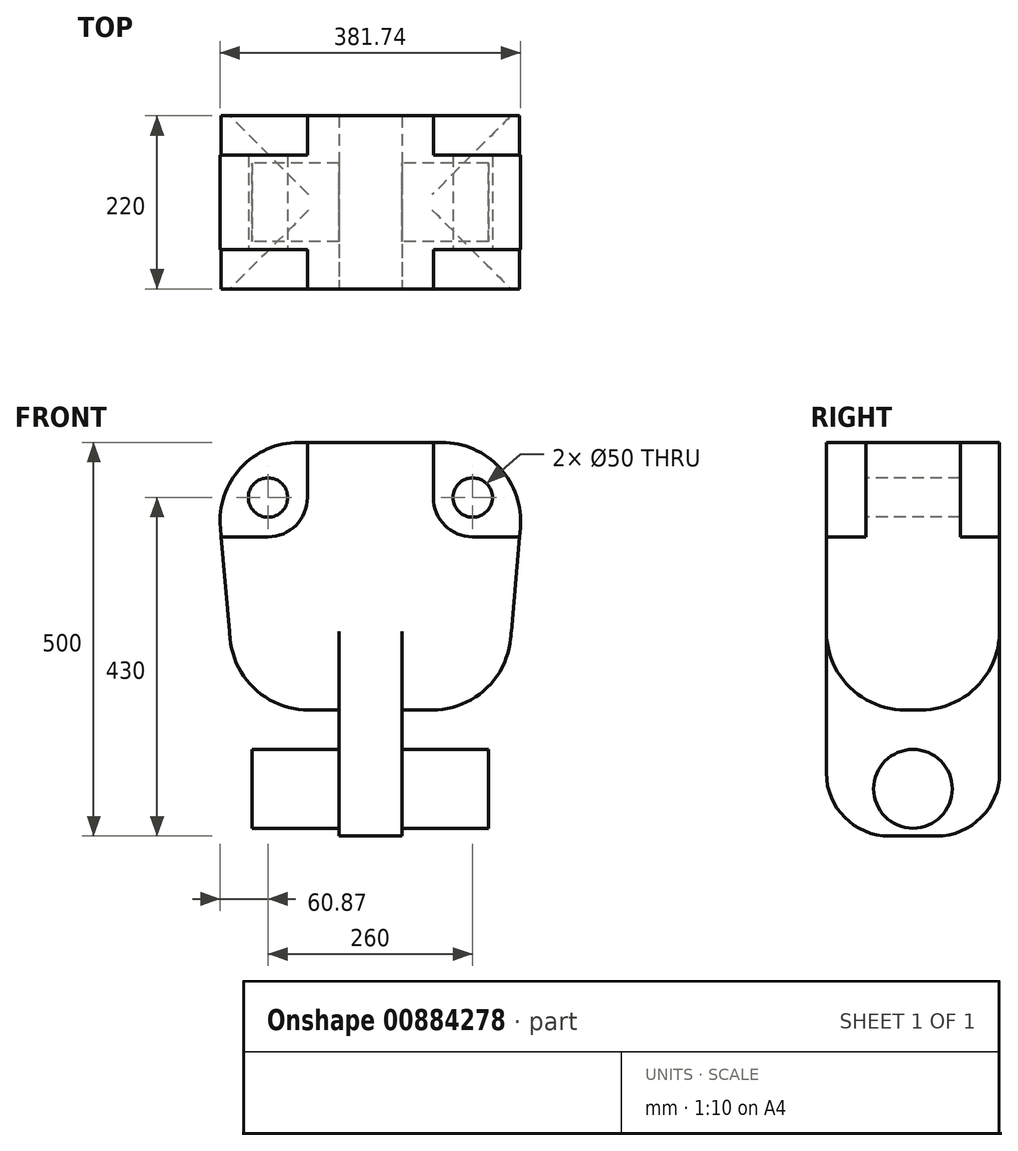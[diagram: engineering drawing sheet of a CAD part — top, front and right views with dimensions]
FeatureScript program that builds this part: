
annotation { "Feature Type Name" : "Feature", "Feature Type Description" : "" }
export const myFeature = defineFeature(function(context is Context, id is Id, definition is map)
    precondition{}
    {
        {
            var Q0;
            Q0=qCreatedBy(makeId("Front.planeOp"),FACE);
            var sketch = newSketch(context, id + "F0", { "sketchPlane" : qUnion([Q0])});
            skLineSegment(sketch, "E0", {"start": v(0, 0) * mm, "end": v(0, 384.02) * mm, "construction": true});
            skLineSegment(sketch, "E1", {"start": v(0, -60) * mm, "end": v(-40, -60) * mm});
            skLineSegment(sketch, "E2", {"start": v(-40, -60) * mm, "end": v(-40, 100) * mm});
            skLineSegment(sketch, "E3", {"start": v(-40, 100) * mm, "end": v(-170.25, 100) * mm});
            skLineSegment(sketch, "E4", {"start": v(-170.25, 100) * mm, "end": v(-200, 440) * mm});
            skLineSegment(sketch, "E5", {"start": v(-200, 440) * mm, "end": v(0, 440) * mm});
            skLineSegment(sketch, "E6.MirrorCS", {"start": v(0, -60) * mm, "end": v(40, -60) * mm});
            skLineSegment(sketch, "E7.MirrorCS", {"start": v(200, 440) * mm, "end": v(0, 440) * mm});
            skLineSegment(sketch, "E8.MirrorCS", {"start": v(40, -60) * mm, "end": v(40, 100) * mm});
            skLineSegment(sketch, "E9.MirrorCS", {"start": v(40, 100) * mm, "end": v(170.25, 100) * mm});
            skLineSegment(sketch, "E10.MirrorCS", {"start": v(170.25, 100) * mm, "end": v(200, 440) * mm});
            skSolve(sketch);
        }
        {
            var Q0;
            Q0 = qSketchRegion(id + "F0", true);
            extrude(context, id + "F1", {"entities" : qUnion([Q0]), "endBound" : BoundingType.SYMMETRIC, "depth" : 220 * mm, "offsetDistance" : 25 * mm});
        }
        {
            var Q0;
            Q0=qCreatedBy(makeId("Front.planeOp"),FACE);
            var sketch = newSketch(context, id + "F2", { "sketchPlane" : qUnion([Q0])});
            skLineSegment(sketch, "E11", {"start": v(4.76, 0) * mm, "end": v(327.19, 0) * mm, "construction": true});
            skLineSegment(sketch, "E12", {"start": v(-150, 50) * mm, "end": v(150, 50) * mm});
            skLineSegment(sketch, "E13", {"start": v(0, 0) * mm, "end": v(0, 285.33) * mm, "construction": true});
            skLineSegment(sketch, "E14", {"start": v(-150, 0) * mm, "end": v(150, 0) * mm});
            skLineSegment(sketch, "E15", {"start": v(-150, 0) * mm, "end": v(-150, 50) * mm});
            skLineSegment(sketch, "E16", {"start": v(150, 0) * mm, "end": v(150, 50) * mm});
            skSolve(sketch);
        }
        {
            var Q0;
            Q0 = qSketchRegion(id + "F2", true);
            var Q1;
            Q1=sQuery(id+"F2.wireOp",EDGE,"E11");
            revolve(context, id + "F3", {"operationType" : NewBodyOperationType.ADD, "surfaceOperationType" : NewSurfaceOperationType.NEW, "entities" : qUnion([Q0]), "axis" : qUnion([Q1]), "revolveType" : RevolveType.FULL});
        }
        {
            var Q0;
            Q0=makeQuery(id+"F1.opExtrude","SWEPT_FACE",FACE,{"disambiguationData":[OSD([sQuery(id+"F0.wireOp",EDGE,"E5"),sQuery(id+"F0.wireOp",EDGE,"E7.MirrorCS")])]});
            var sketch = newSketch(context, id + "F4", { "sketchPlane" : qUnion([Q0])});
            skLineSegment(sketch, "E17.bottom", {"start": v(-200, 110) * mm, "end": v(-80, 110) * mm});
            skLineSegment(sketch, "E17.top", {"start": v(-200, 60) * mm, "end": v(-80, 60) * mm});
            skLineSegment(sketch, "E17.left", {"start": v(-200, 110) * mm, "end": v(-200, 60) * mm});
            skLineSegment(sketch, "E17.right", {"start": v(-80, 110) * mm, "end": v(-80, 60) * mm});
            skLineSegment(sketch, "E18.bottom", {"start": v(-200, -110) * mm, "end": v(-80, -110) * mm});
            skLineSegment(sketch, "E18.top", {"start": v(-200, -60) * mm, "end": v(-80, -60) * mm});
            skLineSegment(sketch, "E18.left", {"start": v(-200, -110) * mm, "end": v(-200, -60) * mm});
            skLineSegment(sketch, "E18.right", {"start": v(-80, -110) * mm, "end": v(-80, -60) * mm});
            skLineSegment(sketch, "E19.bottom", {"start": v(200, -110) * mm, "end": v(80, -110) * mm});
            skLineSegment(sketch, "E19.top", {"start": v(200, -60) * mm, "end": v(80, -60) * mm});
            skLineSegment(sketch, "E19.left", {"start": v(200, -110) * mm, "end": v(200, -60) * mm});
            skLineSegment(sketch, "E19.right", {"start": v(80, -110) * mm, "end": v(80, -60) * mm});
            skLineSegment(sketch, "E20.bottom", {"start": v(200, 110) * mm, "end": v(80, 110) * mm});
            skLineSegment(sketch, "E20.top", {"start": v(200, 60) * mm, "end": v(80, 60) * mm});
            skLineSegment(sketch, "E20.left", {"start": v(200, 110) * mm, "end": v(200, 60) * mm});
            skLineSegment(sketch, "E20.right", {"start": v(80, 110) * mm, "end": v(80, 60) * mm});
            skLineSegment(sketch, "E21", {"start": v(0, 0) * mm, "end": v(276.04, 0) * mm, "construction": true});
            skLineSegment(sketch, "E22", {"start": v(0, 0) * mm, "end": v(0, 138.88) * mm, "construction": true});
            skSolve(sketch);
        }
        {
            var Q0;
            Q0=makeQuery(id+"F4.imprint","IMPRINT",FACE,{"disambiguationData":[TD([[makeQuery(id+"F4.imprint","IMPRINT",EDGE,{"derivedFrom":sQuery(id+"F4.wireOp",EDGE,"E19.bottom")}),-1.0]])]});
            var Q1;
            Q1=makeQuery(id+"F4.imprint","IMPRINT",FACE,{"disambiguationData":[TD([[makeQuery(id+"F4.imprint","IMPRINT",EDGE,{"derivedFrom":sQuery(id+"F4.wireOp",EDGE,"E20.bottom")}),1.0]])]});
            var Q2;
            Q2=makeQuery(id+"F4.imprint","IMPRINT",FACE,{"disambiguationData":[TD([[makeQuery(id+"F4.imprint","IMPRINT",EDGE,{"derivedFrom":sQuery(id+"F4.wireOp",EDGE,"E17.bottom")}),1.0]])]});
            var Q3;
            Q3=makeQuery(id+"F4.imprint","IMPRINT",FACE,{"disambiguationData":[TD([[makeQuery(id+"F4.imprint","IMPRINT",EDGE,{"derivedFrom":sQuery(id+"F4.wireOp",EDGE,"E18.bottom")}),-1.0]])]});
            extrude(context, id + "F5", {"entities" : qUnion([Q0, Q1, Q2, Q3]), "operationType" : NewBodyOperationType.REMOVE, "oppositeDirection" : true, "depth" : 120 * mm, "offsetDistance" : 25 * mm});
        }
        {
            var Q0;
            Q0=makeQuery(id+"F5.boolean.opBoolean","COPY",EDGE,{"derivedFrom":makeQuery(id+"F5.opExtrude","CAP_EDGE",EDGE,{"disambiguationData":[OSD([sQuery(id+"F4.wireOp",EDGE,"E19.right")])],"isStart":false})});
            var Q1;
            Q1=makeQuery(id+"F5.boolean.opBoolean","COPY",EDGE,{"derivedFrom":makeQuery(id+"F5.opExtrude","CAP_EDGE",EDGE,{"disambiguationData":[OSD([sQuery(id+"F4.wireOp",EDGE,"E18.right")])],"isStart":false})});
            var Q2;
            Q2=makeQuery(id+"F5.boolean.opBoolean","COPY",EDGE,{"derivedFrom":makeQuery(id+"F5.opExtrude","CAP_EDGE",EDGE,{"disambiguationData":[OSD([sQuery(id+"F4.wireOp",EDGE,"E17.right")])],"isStart":false})});
            var Q3;
            Q3=makeQuery(id+"F5.boolean.opBoolean","COPY",EDGE,{"derivedFrom":makeQuery(id+"F5.opExtrude","CAP_EDGE",EDGE,{"disambiguationData":[OSD([sQuery(id+"F4.wireOp",EDGE,"E20.right")])],"isStart":false})});
            fillet(context, id + "F6", {"entities" : qUnion([Q0, Q1, Q2, Q3]), "radius" : 50 * mm, "tangentPropagation" : true, "allowEdgeOverflow" : false});
        }
        {
            var Q0;
            Q0=makeQuery(id+"F1.opExtrude","SWEPT_EDGE",EDGE,{"disambiguationData":[OSD([sQuery(id+"F0.wireOp",EDGE,"E7.MirrorCS"),sQuery(id+"F0.wireOp",EDGE,"E10.MirrorCS")])]});
            var Q1;
            Q1=makeQuery(id+"F1.opExtrude","SWEPT_EDGE",EDGE,{"disambiguationData":[OSD([sQuery(id+"F0.wireOp",EDGE,"E4"),sQuery(id+"F0.wireOp",EDGE,"E5")])]});
            var Q2;
            Q2=makeQuery(id+"F1.opExtrude","CAP_EDGE",EDGE,{"disambiguationData":[OSD([sQuery(id+"F0.wireOp",EDGE,"E9.MirrorCS")])],"isStart":false});
            var Q3;
            Q3=makeQuery(id+"F1.opExtrude","SWEPT_EDGE",EDGE,{"disambiguationData":[OSD([sQuery(id+"F0.wireOp",EDGE,"E9.MirrorCS"),sQuery(id+"F0.wireOp",EDGE,"E10.MirrorCS")])]});
            var Q4;
            Q4=makeQuery(id+"F1.opExtrude","CAP_EDGE",EDGE,{"disambiguationData":[OSD([sQuery(id+"F0.wireOp",EDGE,"E9.MirrorCS")])],"isStart":true});
            var Q5;
            Q5=makeQuery(id+"F1.opExtrude","CAP_EDGE",EDGE,{"disambiguationData":[OSD([sQuery(id+"F0.wireOp",EDGE,"E3")])],"isStart":true});
            var Q6;
            Q6=makeQuery(id+"F1.opExtrude","CAP_EDGE",EDGE,{"disambiguationData":[OSD([sQuery(id+"F0.wireOp",EDGE,"E3")])],"isStart":false});
            var Q7;
            Q7=makeQuery(id+"F1.opExtrude","SWEPT_EDGE",EDGE,{"disambiguationData":[OSD([sQuery(id+"F0.wireOp",EDGE,"E3"),sQuery(id+"F0.wireOp",EDGE,"E4")])]});
            fillet(context, id + "F7", {"entities" : qUnion([Q0, Q1, Q2, Q3, Q4, Q5, Q6, Q7]), "radius" : 100 * mm, "tangentPropagation" : true, "allowEdgeOverflow" : false});
        }
        {
            var Q0;
            Q0=qCreatedBy(makeId("Front.planeOp"),FACE);
            var sketch = newSketch(context, id + "F8", { "sketchPlane" : qUnion([Q0])});
            skCircle(sketch, "E23", {"center": v(130, 370) * mm, "radius": 25 * mm});
            skLineSegment(sketch, "E24", {"start": v(0, 0) * mm, "end": v(0, 542.63) * mm, "construction": true});
            skCircle(sketch, "E25.MirrorC", {"center": v(-130, 370) * mm, "radius": 25 * mm});
            skSolve(sketch);
        }
        {
            var Q0;
            Q0 = qSketchRegion(id + "F8", true);
            extrude(context, id + "F9", {"entities" : qUnion([Q0]), "operationType" : NewBodyOperationType.REMOVE, "endBound" : BoundingType.THROUGH_ALL, "oppositeDirection" : true, "depth" : 25 * mm, "offsetDistance" : 25 * mm, "hasSecondDirection" : true, "secondDirectionBound" : SecondDirectionBoundingType.THROUGH_ALL, "secondDirectionOppositeDirection" : false, "secondDirectionDepth" : 25 * mm});
        }
        {
            var Q0;
            Q0=makeQuery(id+"F1.opExtrude","CAP_EDGE",EDGE,{"disambiguationData":[OSD([sQuery(id+"F0.wireOp",EDGE,"E1"),sQuery(id+"F0.wireOp",EDGE,"E6.MirrorCS")])],"isStart":false});
            var Q1;
            Q1=makeQuery(id+"F1.opExtrude","CAP_EDGE",EDGE,{"disambiguationData":[OSD([sQuery(id+"F0.wireOp",EDGE,"E1"),sQuery(id+"F0.wireOp",EDGE,"E6.MirrorCS")])],"isStart":true});
            fillet(context, id + "F10", {"entities" : qUnion([Q0, Q1]), "radius" : 80 * mm, "tangentPropagation" : true, "allowEdgeOverflow" : false});
        }
    });
